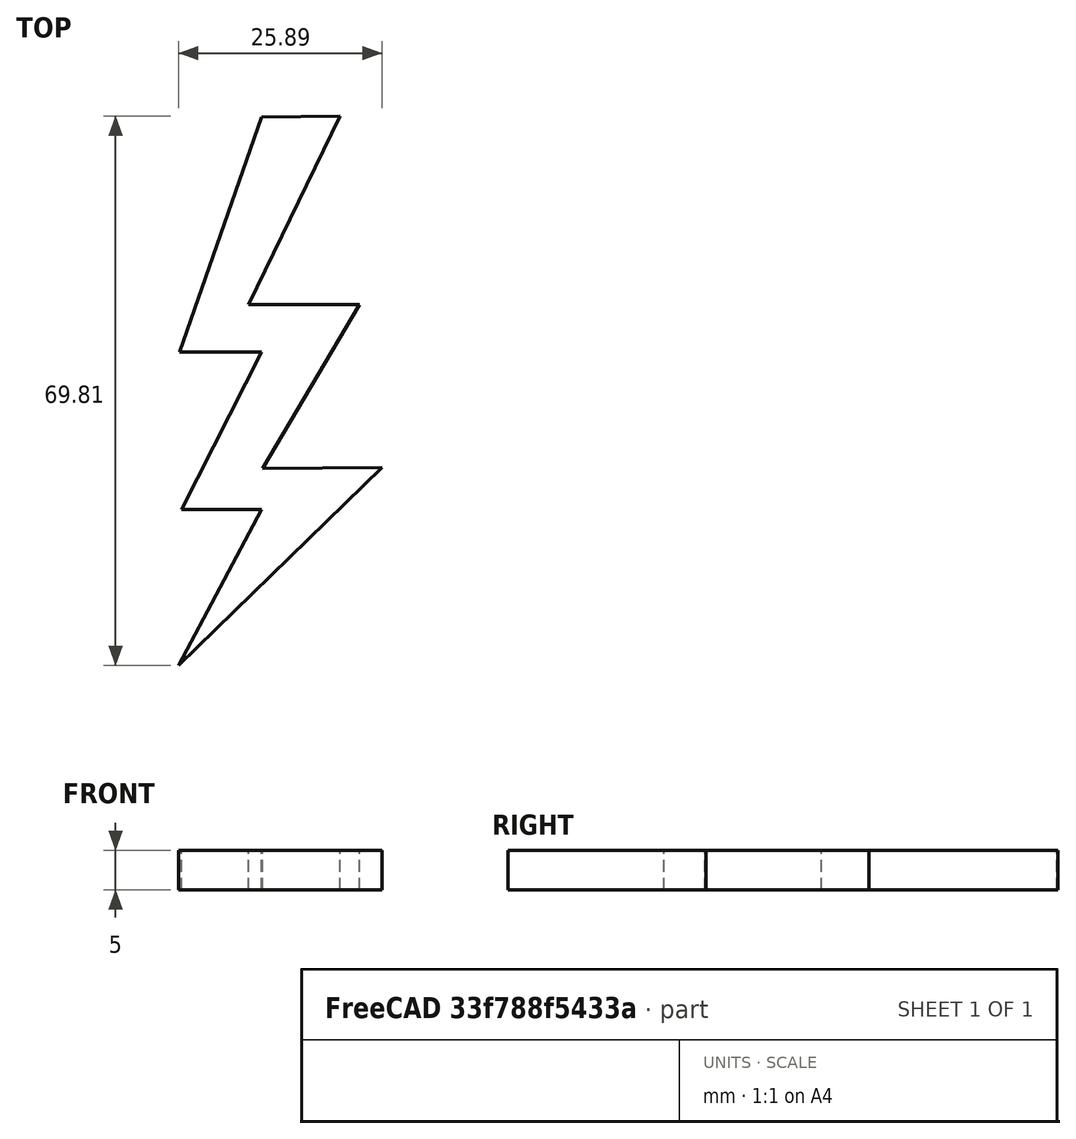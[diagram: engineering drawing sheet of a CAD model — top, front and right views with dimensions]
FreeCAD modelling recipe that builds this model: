
FCSTD DOCUMENT  (FreeCAD 0.21R33771 (Git))
Label: OJT1_T16R03_llampec
License: All rights reserved
LicenseURL: http://en.wikipedia.org/wiki/All_rights_reserved
objects: Sketcher::SketchObject×1, PartDesign::Pad×1, PartDesign::Body×1
note: 4 computed .brp shape members not serialized (recipe doc carries the construction recipe); baked Part::Feature solids carry a one-line shape summary decoded from their .brp

FEATURE [Sketcher::SketchObject] Sketch
  FullyConstrained = false
  MapMode = 5
  Support = -> [XY_Plane]
  sketch-geometry (11):
    g0: LineSegment StartX=20.1205 StartY=69.6703 StartZ=0 EndX=9.70953 EndY=39.8073 EndZ=0
    g1: LineSegment StartX=9.70953 StartY=39.8073 StartZ=0 EndX=20.1205 EndY=39.8073 EndZ=0
    g2: LineSegment StartX=20.1205 StartY=39.8073 StartZ=0 EndX=9.9835 EndY=19.8073 EndZ=0
    g3: LineSegment StartX=9.9835 StartY=19.8073 StartZ=0 EndX=20.1205 EndY=19.8073 EndZ=0
    g4: LineSegment StartX=20.1205 StartY=19.8073 StartZ=0 EndX=9.57254 EndY=0 EndZ=0
    g5: LineSegment StartX=9.57254 StartY=0 StartZ=0 EndX=35.463 EndY=25.1498 EndZ=0
    g6: LineSegment StartX=35.463 StartY=25.1498 StartZ=0 EndX=20.2575 EndY=25.0128 EndZ=0
    g7: LineSegment StartX=20.2575 StartY=25.0128 StartZ=0 EndX=32.5862 EndY=45.8347 EndZ=0
    g8: LineSegment StartX=32.5862 StartY=45.8347 StartZ=0 EndX=18.4767 EndY=45.8347 EndZ=0
    g9: LineSegment StartX=18.4767 StartY=45.8347 StartZ=0 EndX=30.1205 EndY=69.8073 EndZ=0
    g10: LineSegment StartX=30.1205 StartY=69.8073 StartZ=0 EndX=20.1205 EndY=69.6703 EndZ=0
  constraints (11):
    c: Coincident(g0,g1)
    c: Coincident(g1,g2)
    c: Coincident(g2,g3)
    c: Coincident(g3,g4)
    c: Coincident(g4,g5)
    c: Coincident(g5,g6)
    c: Coincident(g6,g7)
    c: Coincident(g7,g8)
    c: Coincident(g8,g9)
    c: Coincident(g9,g10)
    c: Coincident(g10,g0)
FEATURE [PartDesign::Pad] Pad
  Direction = (0,0,1)
  Length = 5
  Length2 = 10
  Profile = -> Sketch
  ReferenceAxis = -> Sketch [N_Axis]
  Type = 0
FEATURE [PartDesign::Body] Body
  Group = -> [Sketch,Pad]
  Origin = -> Origin
  Tip = -> Pad
